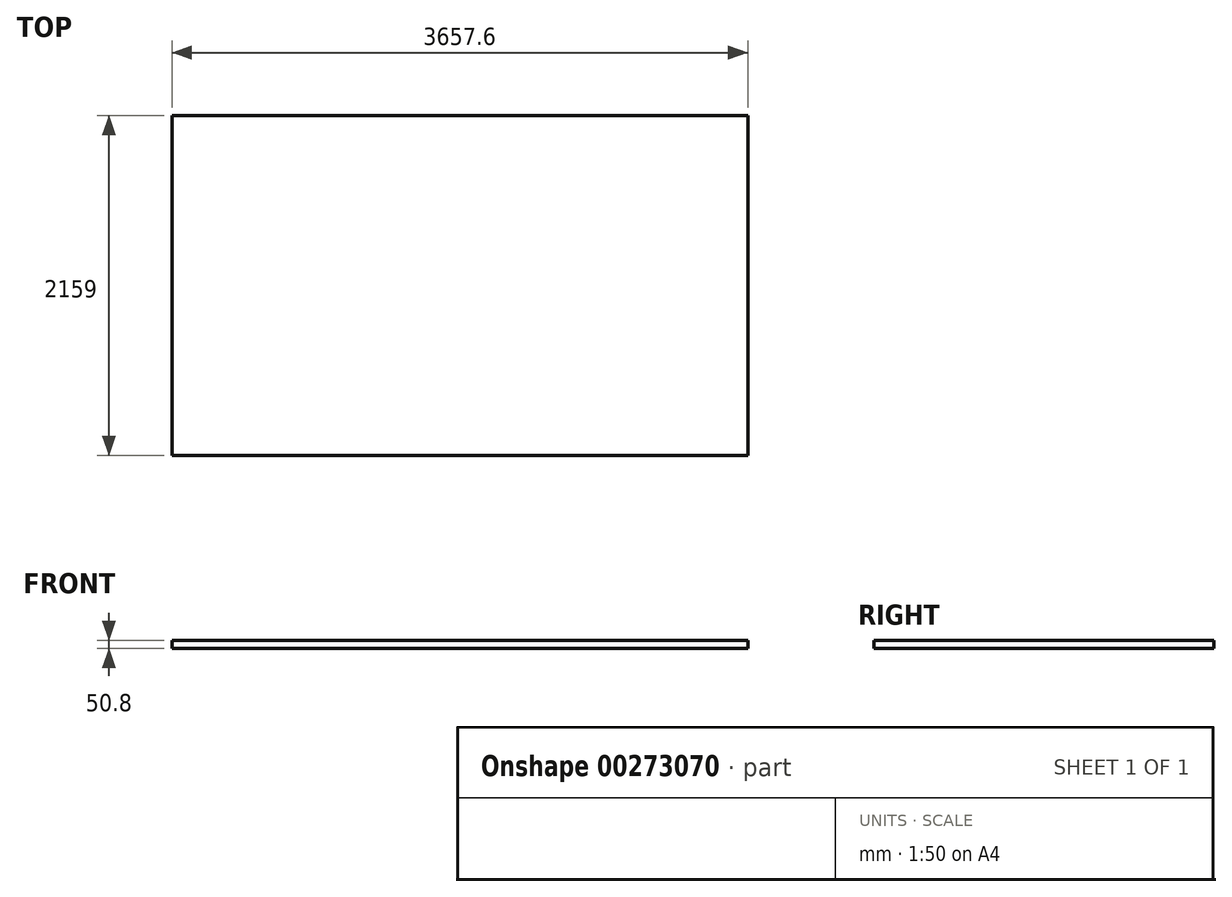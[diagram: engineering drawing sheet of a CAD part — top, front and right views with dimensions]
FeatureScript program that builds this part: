
annotation { "Feature Type Name" : "Feature", "Feature Type Description" : "" }
export const myFeature = defineFeature(function(context is Context, id is Id, definition is map)
    precondition{}
    {
        {
            var Q0;
            Q0=qCreatedBy(makeId("Top.planeOp"),FACE);
            var sketch = newSketch(context, id + "F0", { "sketchPlane" : qUnion([Q0])});
            skLineSegment(sketch, "E0.bottom", {"start": v(-1411.21, 1075.74) * mm, "end": v(2246.39, 1075.74) * mm});
            skLineSegment(sketch, "E0.top", {"start": v(-1411.21, -1083.26) * mm, "end": v(2246.39, -1083.26) * mm});
            skLineSegment(sketch, "E0.left", {"start": v(-1411.21, 1075.74) * mm, "end": v(-1411.21, -1083.26) * mm});
            skLineSegment(sketch, "E0.right", {"start": v(2246.39, 1075.74) * mm, "end": v(2246.39, -1083.26) * mm});
            skSolve(sketch);
        }
        {
            var Q0;
            Q0 = qSketchRegion(id + "F0", true);
            extrude(context, id + "F1", {"entities" : qUnion([Q0]), "depth" : 50.8 * mm});
        }
    });
